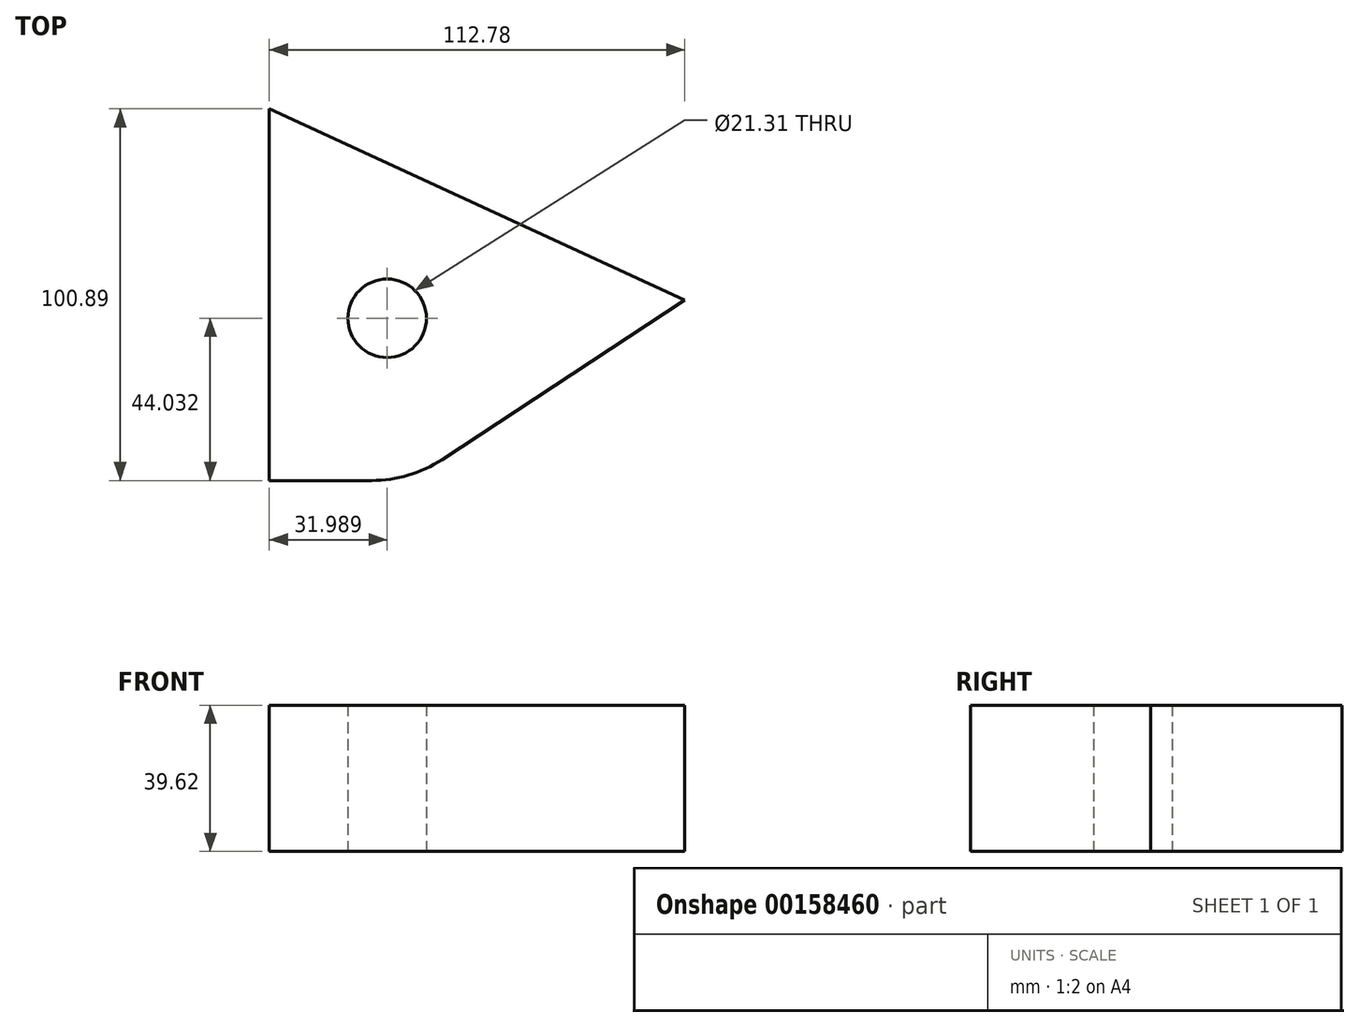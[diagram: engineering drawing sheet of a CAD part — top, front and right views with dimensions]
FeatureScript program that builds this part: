
annotation { "Feature Type Name" : "Feature", "Feature Type Description" : "" }
export const myFeature = defineFeature(function(context is Context, id is Id, definition is map)
    precondition{}
    {
        {
            var Q0;
            Q0=qCreatedBy(makeId("Top.planeOp"),FACE);
            var sketch = newSketch(context, id + "F0", { "sketchPlane" : qUnion([Q0])});
            skLineSegment(sketch, "E0", {"start": v(-18.14, 64.82) * mm, "end": v(-19.33, -35.26) * mm, "construction": true});
            skLineSegment(sketch, "E1", {"start": v(-115.7, -35.42) * mm, "end": v(-115.7, 13.27) * mm});
            skLineSegment(sketch, "E2", {"start": v(-115.7, 13.27) * mm, "end": v(-86.47, 44.5) * mm});
            skLineSegment(sketch, "E3", {"start": v(-86.47, 44.5) * mm, "end": v(-35.73, 23.34) * mm});
            skLineSegment(sketch, "E4", {"start": v(-35.73, 23.34) * mm, "end": v(-86.47, -35.42) * mm});
            skLineSegment(sketch, "E5", {"start": v(-86.47, -35.42) * mm, "end": v(-115.7, -35.42) * mm});
            skLineSegment(sketch, "E6", {"start": v(0, 0) * mm, "end": v(0, 100.9) * mm});
            skLineSegment(sketch, "E7", {"start": v(0, 100.9) * mm, "end": v(112.78, 48.95) * mm});
            skLineSegment(sketch, "E8", {"start": v(112.78, 48.95) * mm, "end": v(38.18, 0) * mm});
            skLineSegment(sketch, "E9", {"start": v(38.18, 0) * mm, "end": v(0, 0) * mm});
            skSolve(sketch);
        }
        {
            var Q0;
            Q0=makeQuery(id+"F0.imprint","IMPRINT",FACE,{"disambiguationData":[TD([[makeQuery(id+"F0.imprint","IMPRINT",EDGE,{"derivedFrom":sQuery(id+"F0.wireOp",EDGE,"E6")}),-1.0]])]});
            extrude(context, id + "F1", {"entities" : qUnion([Q0]), "depth" : 39.62 * mm});
        }
        {
            var Q0;
            Q0=makeQuery(id+"F1.opExtrude","SWEPT_EDGE",EDGE,{"disambiguationData":[OSD([sQuery(id+"F0.wireOp",EDGE,"E8"),sQuery(id+"F0.wireOp",EDGE,"E9")])]});
            fillet(context, id + "F2", {"entities" : qUnion([Q0]), "radius" : 34.9 * mm, "tangentPropagation" : true, "allowEdgeOverflow" : false});
        }
        {
            var Q0;
            Q0=qCreatedBy(makeId("Top.planeOp"),FACE);
            var sketch = newSketch(context, id + "F3", { "sketchPlane" : qUnion([Q0])});
            skCircle(sketch, "E10", {"center": v(31.99, 44.03) * mm, "radius": 10.66 * mm});
            skSolve(sketch);
        }
        {
            var Q0;
            Q0=makeQuery(id+"F3.imprint","IMPRINT",FACE,{"disambiguationData":[TD([[makeQuery(id+"F3.imprint","IMPRINT",EDGE,{"derivedFrom":sQuery(id+"F3.wireOp",EDGE,"E10")}),1.0]])]});
            extrude(context, id + "F4", {"entities" : qUnion([Q0]), "operationType" : NewBodyOperationType.REMOVE, "depth" : 91.19 * mm});
        }
    });
